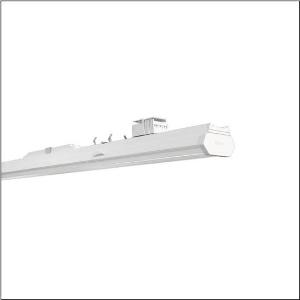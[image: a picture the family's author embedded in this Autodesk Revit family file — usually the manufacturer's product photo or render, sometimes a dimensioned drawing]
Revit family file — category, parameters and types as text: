
# Revit family: licross_21_protected_ho_52td12dn4e5md
name_source: partatom
category: Lighting Fixtures
units: mm (PartAtom-declared; Revit-internal decimal feet)

## family parameters
Cut with Voids When Loaded = No
Host = Face
Light Source = No
Part Type = Normal
Room Calculation Point = No
Round Connector Dimension = Use Diameter
Shared = No

## types (1)
- --- (1 x LED, 2200 lm, 14.2 W, 4000K)
    Apparent Load = 14 VA
    CIE Flux Codes = 70 91 97 98 100
    Color Rendering = 80
    Color Temperature = 4000K
    Default Elevation = 1800 mm
    Description = Licross 21 Protected HO, luminaire insert, of sheet steel, galvanised, coil coated, white, length: 1.500mm, width: 90mm, height: 103mm, LED rated luminous flux: 14.690lm, light colour: 840, SDCM (Standard Deviation of Colour Matching)MacAdam ≤ 3 SDCM (initial), control gear: DALI 2 (for two DALI lines), with plug, 6-pole, with phase selection, mains connection: 220..240V, AC/DC, 0/50..60Hz, rated input power: 85W, without changeover relay, for emergency light function, for central battery installations according to EN 60598-2-22, internal wiring halogen-free, primary light control with lens, of plastic, primary optical cover: cover, of PMMA, light emission: direct distribution, primary light characteristic: symmetric, protection rating (complete): IP54, insulation class (complete): insulation class I (protective earthing), certification: CE, ENEC, VDE, UKCA, protection symbol: D if used in an environment with non-conductive dust loads with corresponding accessories, impact resistance: IK06, permissible ambient temperature for indoor applications: -25..+35°C, standard: EN 60598-2-22, corresponds to IFS (International Featured Standards) requirements for safety and quality in the food industry, reducing of maximum allowable ambient temperature of 5°C with ceiling mounting, LABS conformity tested according to VDMA 24364:2018-05, The light source and the operating device comply with the requirements of the Ecodesign Regulation (EU) 2019/2020 and are replaceable in accordance with this regulation, packaging unit: 1 piece
    Height = 92 mm
    Lamp = 1 x LED
    Lamp Light Flux = 2200 lm
    Lamp Power = 14.2 W
    Lamp count = 1
    Length = 1500 mm
    Luminous efficacy = 155 lm/W
    Manufacturer = Siteco
    ModVariant = No
    Model = 52TD12DN4E5MD
    Mounting Place = Ceiling
    Mounting Type = Pendant
    Number of Poles = 1
    OnlyDefault = Yes
    Power Factor = 1
    Product Name = Licross 21 Protected HO
    Product group = luminaire insert | ceiling pendant
    ProductGroupID = 901
    Protection Class = Protection class I
    Protection Degree = IP 54
    RLX_Detail_Level = 1
    RLX_Emergency_Light_Flux = 0 lm
    RLX_Emergency_Type = 0
    RLX_Emergency_Type_DB = No
    RlxData = <blob elided: 25169 chars, md5=099ff6e5>
    Socket = socket
    Standby Power = 0 W
    System Light Flux = 2200 lm
    System Power = 14 W
    Type Comments = : DC mode (central or group accumulator) initial emergency light level
    Type Image = l_1256148.jpg
    URL = http://relux.com
    VarID = @adj_118071
    Voltage = 0 V
    Weight = 0.00 kg
    Width = 88 mm

## geometry (parser evidence)
native form markers: Blend x4, Sweep x10
no freeform markers — native parametric forms only
